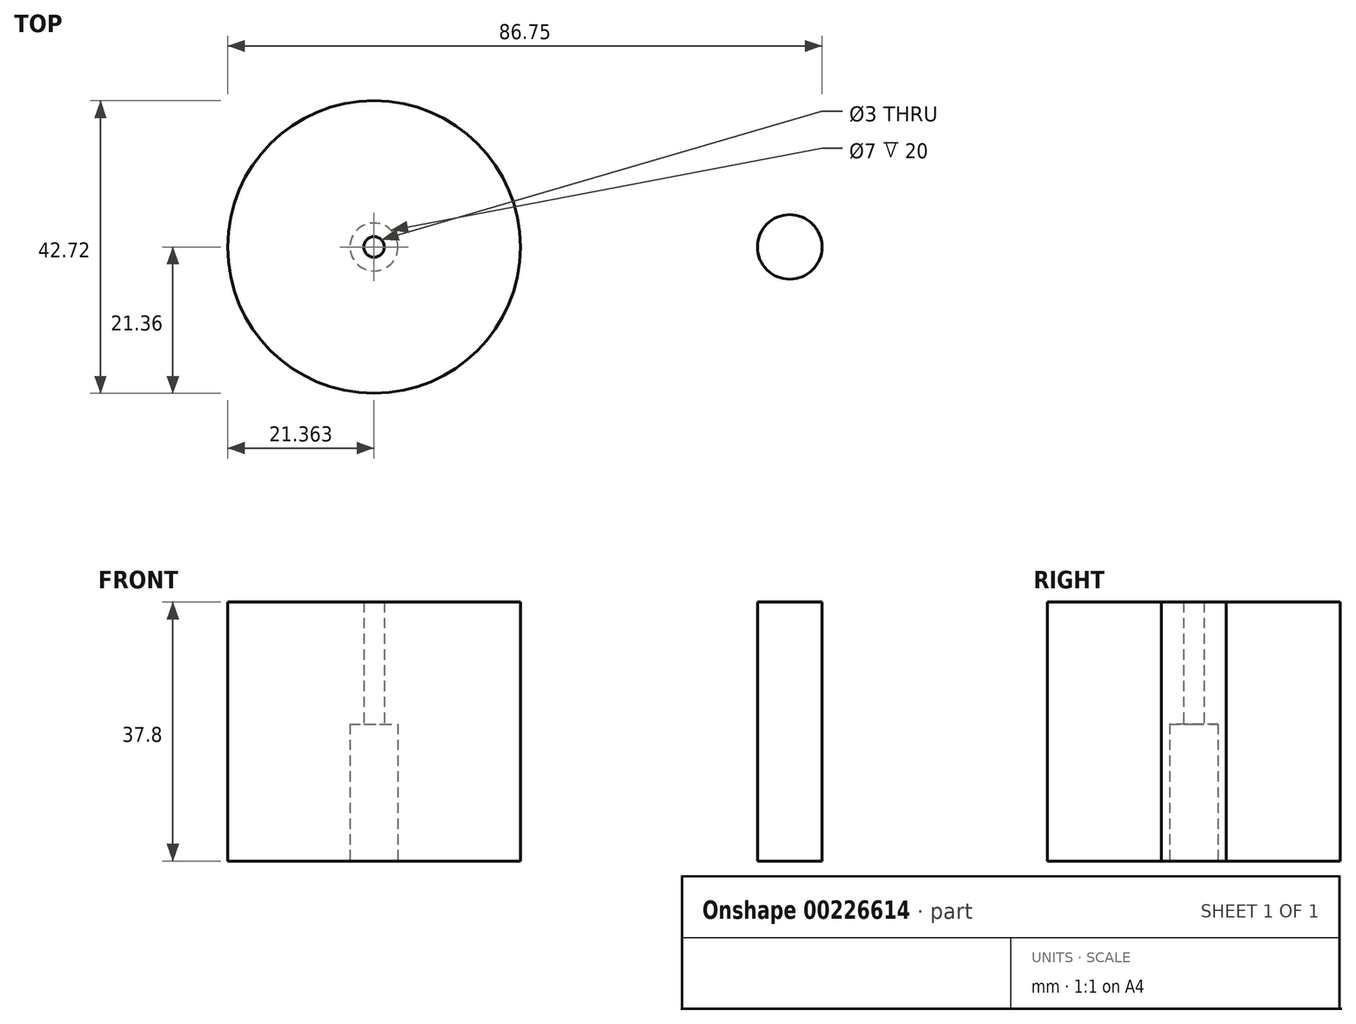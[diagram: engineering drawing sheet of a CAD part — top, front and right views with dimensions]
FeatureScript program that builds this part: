
annotation { "Feature Type Name" : "Feature", "Feature Type Description" : "" }
export const myFeature = defineFeature(function(context is Context, id is Id, definition is map)
    precondition{}
    {
        {
            var Q0;
            Q0=qCreatedBy(makeId("Top.planeOp"),FACE);
            var sketch = newSketch(context, id + "F0", { "sketchPlane" : qUnion([Q0])});
            skCircle(sketch, "E0", {"center": v(-34.64, 0) * mm, "radius": 21.36 * mm});
            skCircle(sketch, "E1", {"center": v(26.04, 0) * mm, "radius": 12.25 * mm});
            skCircle(sketch, "E2", {"center": v(26.04, 0) * mm, "radius": 4.71 * mm});
            skSolve(sketch);
        }
        {
            var Q0;
            Q0=makeQuery(id+"F0.imprint","IMPRINT",FACE,{"disambiguationData":[TD([[makeQuery(id+"F0.imprint","IMPRINT",EDGE,{"derivedFrom":sQuery(id+"F0.wireOp",EDGE,"E0")}),1.0]])]});
            extrude(context, id + "F1", {"entities" : qUnion([Q0]), "depth" : 37.8 * mm});
        }
        {
            var Q0;
            Q0=makeQuery(id+"F0.imprint","IMPRINT",FACE,{"disambiguationData":[TD([[makeQuery(id+"F0.imprint","IMPRINT",EDGE,{"derivedFrom":sQuery(id+"F0.wireOp",EDGE,"E2")}),1.0]])]});
            var Q1;
            Q1=makeQuery(id+"F1.opExtrude","CAP_FACE",FACE,{"disambiguationData":[OSD([sQuery(id+"F0.wireOp",EDGE,"E0")])],"isStart":false});
            extrude(context, id + "F2", {"entities" : qUnion([Q0]), "endBound" : BoundingType.UP_TO_SURFACE, "endBoundEntityFace" : qUnion([Q1]), "depth" : 10.4 * mm});
        }
        {
            var Q0;
            Q0=sQuery(id+"F0.wireOp",VERTEX,"E0.center");
            var Q1;
            Q1=makeQuery(id+"F1.opExtrude","SWEPT_BODY",BODY,{"disambiguationData":[OSD([sQuery(id+"F0.wireOp",EDGE,"E0")])]});
            hole(context, id + "F3", {"style" : HoleStyle.C_BORE, "endStyle" : HoleEndStyle.THROUGH, "oppositeDirection" : true, "holeDiameter" : 3 * mm, "cBoreDiameter" : 7 * mm, "cBoreDepth" : 20 * mm, "locations" : qUnion([Q0]), "scope" : qUnion([Q1]), "isTappedThrough" : true});
        }
    });
